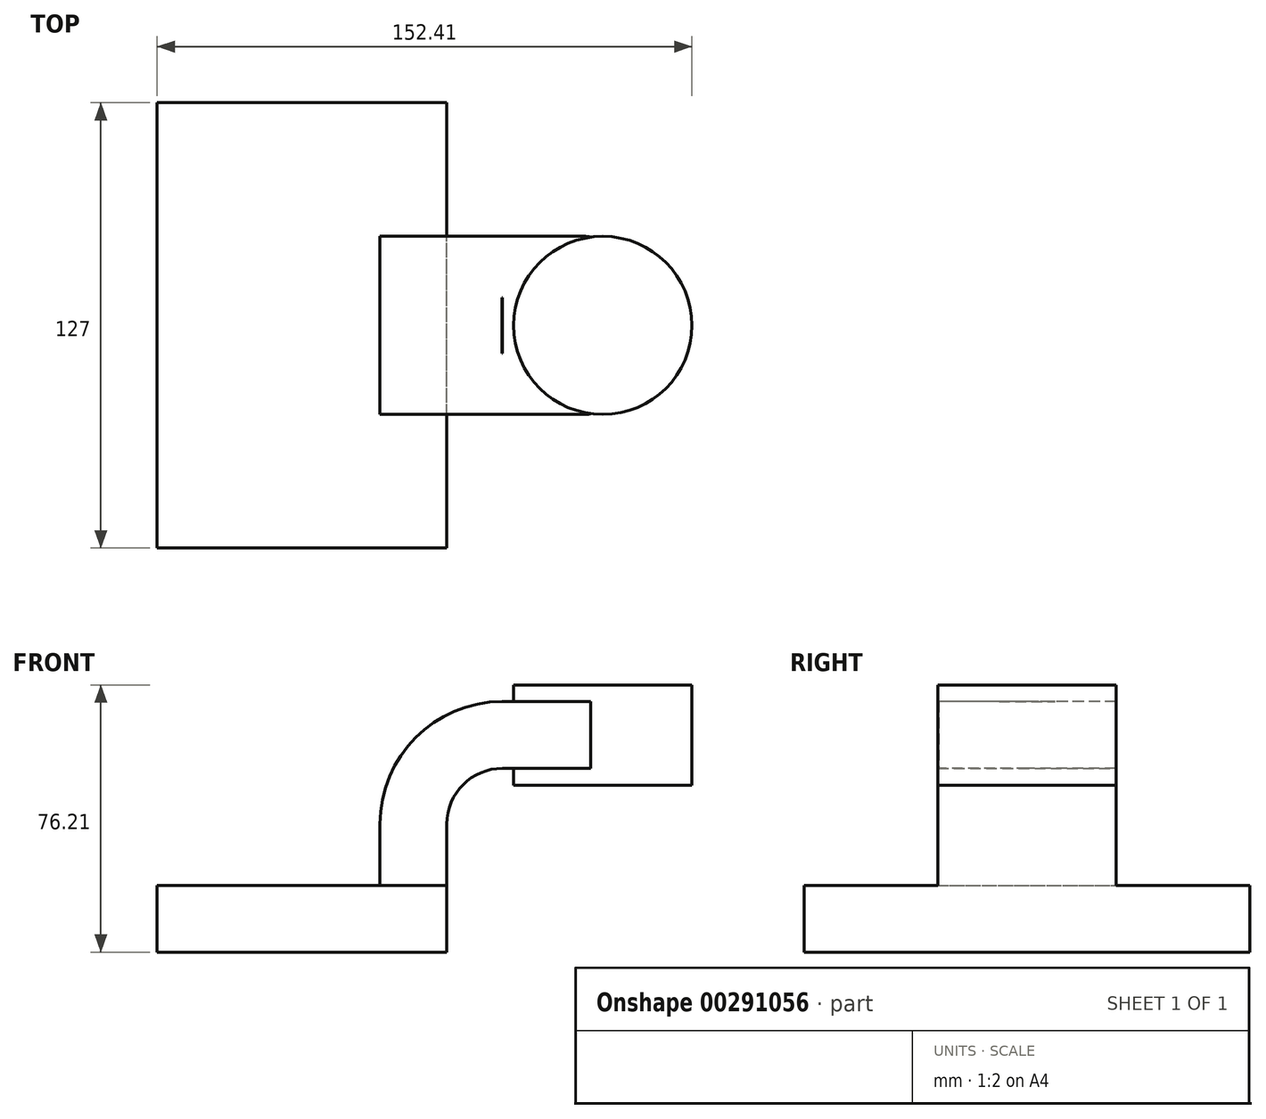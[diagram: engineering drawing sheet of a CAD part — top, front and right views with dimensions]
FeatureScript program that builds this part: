
annotation { "Feature Type Name" : "Feature", "Feature Type Description" : "" }
export const myFeature = defineFeature(function(context is Context, id is Id, definition is map)
    precondition{}
    {
        {
            var Q0;
            Q0=qCreatedBy(makeId("Front.planeOp"),FACE);
            var sketch = newSketch(context, id + "F0", { "sketchPlane" : qUnion([Q0])});
            skLineSegment(sketch, "E0.bottom", {"start": v(41.27, 9.53) * mm, "end": v(-41.28, 9.53) * mm});
            skLineSegment(sketch, "E0.top", {"start": v(41.27, -9.53) * mm, "end": v(-41.28, -9.53) * mm});
            skLineSegment(sketch, "E0.left", {"start": v(-41.28, 9.53) * mm, "end": v(-41.28, -9.52) * mm});
            skLineSegment(sketch, "E0.right", {"start": v(41.27, 9.53) * mm, "end": v(41.27, -9.53) * mm});
            skPoint(sketch, "E0.middle", {"position": v(0, 0) * mm});
            skLineSegment(sketch, "E1.bottom", {"start": v(111.12, 38.1) * mm, "end": v(60.32, 38.1) * mm});
            skLineSegment(sketch, "E1.top", {"start": v(111.12, 66.67) * mm, "end": v(60.32, 66.67) * mm});
            skLineSegment(sketch, "E1.left", {"start": v(111.12, 38.1) * mm, "end": v(111.12, 66.67) * mm});
            skLineSegment(sketch, "E1.right", {"start": v(60.32, 38.1) * mm, "end": v(60.32, 66.67) * mm});
            skPoint(sketch, "E1.middle", {"position": v(85.72, 52.39) * mm});
            skLineSegment(sketch, "E2", {"start": v(41.27, 9.53) * mm, "end": v(41.27, 27) * mm});
            skArc(sketch, "E3", {"start": v(41.27, 27) * mm, "mid": v(45.92, 38.23) * mm, "end": v(57.15, 42.88) * mm});
            skLineSegment(sketch, "E4", {"start": v(57.15, 42.88) * mm, "end": v(85.72, 42.88) * mm});
            skLineSegment(sketch, "E5.0", {"start": v(57.15, 61.93) * mm, "end": v(85.72, 61.93) * mm});
            skArc(sketch, "E5.1", {"start": v(22.22, 27) * mm, "mid": v(32.45, 51.7) * mm, "end": v(57.15, 61.93) * mm});
            skLineSegment(sketch, "E5.2", {"start": v(22.22, 9.53) * mm, "end": v(22.22, 27) * mm});
            skLineSegment(sketch, "E6", {"start": v(85.72, 38.1) * mm, "end": v(85.72, 66.67) * mm});
            skFitSpline(sketch, "E7", {"points": [v(-41.28, 9.53) * mm, v(57.15, 61.93) * mm], "startDerivative": vector(0.9, 105.1) * mm, "endDerivative": vector(142.21, 0.28) * mm});
            skSolve(sketch);
        }
        {
            var Q0;
            Q0=makeQuery(id+"F0.imprint","IMPRINT",FACE,{"disambiguationData":[TD([[makeQuery(id+"F0.imprint","IMPRINT",EDGE,{"derivedFrom":sQuery(id+"F0.wireOp",EDGE,"E0.top")}),-1.0]])]});
            extrude(context, id + "F1", {"entities" : qUnion([Q0]), "endBound" : BoundingType.SYMMETRIC, "depth" : 127 * mm});
        }
        {
            var Q0;
            {var subQ1=sQuery(id+"F0.wireOp",EDGE,"E2");Q0=makeQuery(id+"F0.imprint","IMPRINT",FACE,{"disambiguationData":[TD([[makeQuery(id+"F0.imprint","IMPRINT",EDGE,{"derivedFrom":subQ1}),1.0]])]});}
            var Q1;
            {var subQ0=sQuery(id+"F0.wireOp",EDGE,"E4");var subQ1=sQuery(id+"F0.wireOp",EDGE,"E1.right");var subQ2=makeQuery(id+"F0.imprint","INTERSECT",VERTEX,{"derivedFrom":[subQ1,subQ0]});Q1=makeQuery(id+"F0.imprint","IMPRINT",FACE,{"disambiguationData":[TD([[makeQuery(id+"F0.imprint","IMPRINT",EDGE,{"disambiguationData":[TD([[subQ2,-1.0]])],"derivedFrom":subQ1}),-1.0]])]});}
            extrude(context, id + "F2", {"entities" : qUnion([Q0, Q1]), "operationType" : NewBodyOperationType.ADD, "endBound" : BoundingType.SYMMETRIC, "depth" : 50.8 * mm});
        }
        {
            var Q0;
            Q0=makeQuery(id+"F0.imprint","IMPRINT",FACE,{"disambiguationData":[TD([[makeQuery(id+"F0.imprint","IMPRINT",EDGE,{"derivedFrom":sQuery(id+"F0.wireOp",EDGE,"E5.1")}),1.0]])]});
            extrude(context, id + "F3", {"entities" : qUnion([Q0]), "endBound" : BoundingType.SYMMETRIC, "depth" : 15.88 * mm});
        }
        {
            var Q0;
            Q0=makeQuery(id+"F2.opExtrude","CAP_EDGE",EDGE,{"disambiguationData":[OSD([sQuery(id+"F0.wireOp",EDGE,"E6")])],"isStart":false});
            var Q1;
            Q1=makeQuery(id+"F2.opExtrude","CAP_EDGE",EDGE,{"disambiguationData":[OSD([sQuery(id+"F0.wireOp",EDGE,"E6")])],"isStart":true});
            fillet(context, id + "F4", {"entities" : qUnion([Q0, Q1]), "radius" : 5.08 * mm, "tangentPropagation" : true, "allowEdgeOverflow" : false});
        }
        {
            var Q0;
            {var subQ4=sQuery(id+"F0.wireOp",EDGE,"E1.left");Q0=makeQuery(id+"F0.imprint","IMPRINT",FACE,{"disambiguationData":[TD([[makeQuery(id+"F0.imprint","IMPRINT",EDGE,{"derivedFrom":subQ4}),1.0]])]});}
            var Q1;
            Q1=sQuery(id+"F0.wireOp",EDGE,"E6");
            revolve(context, id + "F5", {"operationType" : NewBodyOperationType.ADD, "entities" : qUnion([Q0]), "axis" : qUnion([Q1]), "revolveType" : RevolveType.FULL});
        }
    });
